# Revit family: Etixx37_ep200_R5-3
name_source: partatom
category: Equipement spécialisé
revit_build: Autodesk Revit Architecture 2016 (Build: 20150220_1215(x64)
units: mm (PartAtom-declared; Revit-internal decimal feet)

## family parameters
Basée sur le plan de construction = Non
Cote de connecteur circulaire = Utiliser le diamètre
Couper avec des vides une fois chargée = Non
Partagée = Non
Point de calcul de pièce = Non
Toujours verticalement = Oui
Type d'élément = Normal

## types (1)
- Etixx37_ep200_R5-3
    Conductivité thermique = 0.0310 W/(m·K)
    Coût = 0 $
    Description = Etixx37 épaisseur 200
    Epaisseur = 200 mm  [stored 0.656168 ft]
    Fabricant = Isobox
    Image du type = Image_Etixx37.jpg
    Matériaux = Isolant PSE Etixx 37
    Modèle = ep : 200mm
    Résistance thermique = 5.3000 (m²·K)/W
    Transmission de la vapeur d’eau (μ) = 20-40
    URL = https://www.isobox-isolation.fr

note: [stored X ft] marks values corroborated as IEEE doubles in the binary element streams (Revit-internal decimal feet)

## geometry (parser evidence)
native form markers: Blend x12
no freeform markers — native parametric forms only
